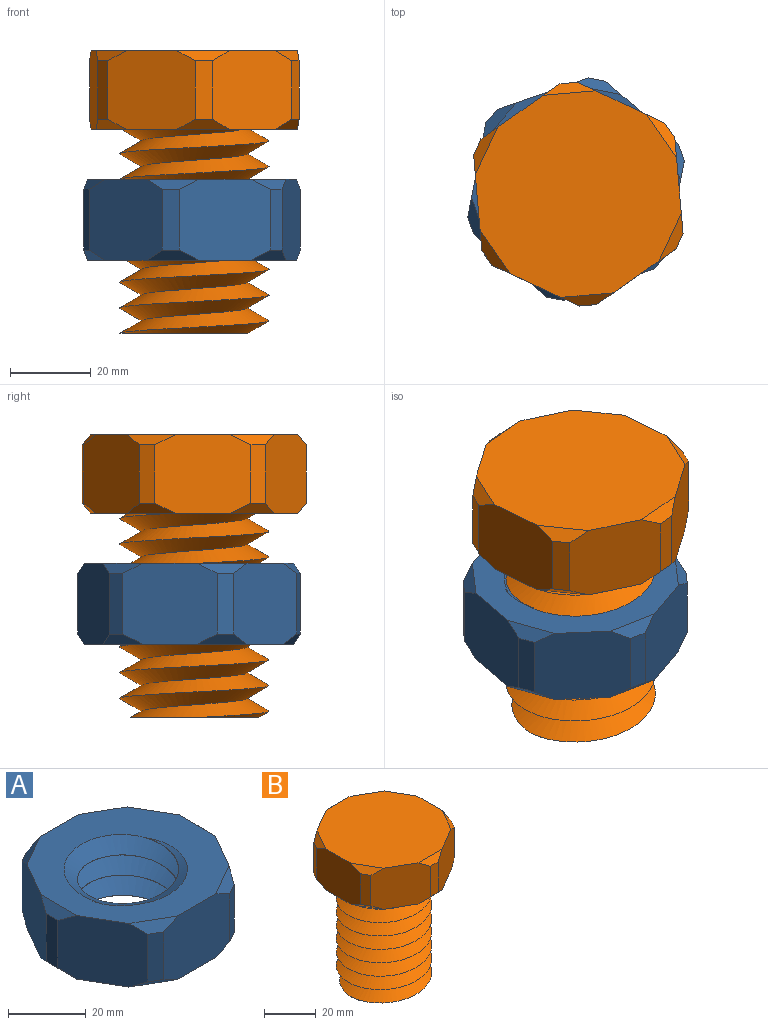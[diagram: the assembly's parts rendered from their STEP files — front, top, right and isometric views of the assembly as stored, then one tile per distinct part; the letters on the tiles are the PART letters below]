
ASSEMBLY  parts=2 mates=1
PART A: 29 faces, bbox 55.2x50x27.6 mm
  f0: cylinder r=13mm len=26mm, axis (0,0,-1), area 3.5mm2, adj f1,f2,f9,f10
  f1: bspline ~42.72x37mm, area 1977mm2, adj f0,f2,f9,f10
  f2: bspline ~42.72x37mm, area 1977.1mm2, adj f0,f1,f9,f10
  f3: plane 20.67x20mm, normal (0.87,-0.5,0), area 452.4mm2, adj f9,f10,f13,f14,f19,f20,f26,f27
  f4: plane 20.67x20mm, normal (0.87,0.5,0), area 452.4mm2, adj f9,f10,f12,f13,f18,f19,f25,f26
  f5: plane 23.87x20mm, normal (0,1,0), area 452.4mm2, adj f9,f10,f11,f12,f17,f18,f24,f25
  f6: plane 20.67x20mm, normal (-0.87,0.5,0), area 452.4mm2, adj f9,f10,f11,f15,f17,f22,f23,f24
  f7: plane 20.67x20mm, normal (-0.87,-0.5,0), area 452.4mm2, adj f9,f10,f15,f16,f21,f22,f23,f28
  f8: plane 23.87x20mm, normal (0,-1,0), area 452.4mm2, adj f9,f10,f14,f16,f20,f21,f27,f28
  f9: plane 50.24x50mm, normal (0,0,1), area 1232.2mm2, adj f0,f1,f2,f3,f4,f5,f6,f7
  f10: plane 50.24x50mm, normal (0,0,-1), area 1232.4mm2, adj f0,f1,f2,f3,f4,f5,f6,f7
  f11: plane 15x3.75mm, normal (-0.5,0.87,0), area 65mm2, adj f5,f6,f17,f24
  f12: plane 15x3.75mm, normal (0.5,0.87,0), area 65mm2, adj f4,f5,f18,f25
  f13: plane 15x4.33mm, normal (1,0,0), area 65mm2, adj f3,f4,f19,f26
  f14: plane 15x3.75mm, normal (0.5,-0.87,0), area 65mm2, adj f3,f8,f20,f27
  f15: plane 15x4.33mm, normal (-1,0,0), area 65mm2, adj f6,f7,f22,f23
  f16: plane 15x3.75mm, normal (-0.5,-0.87,0), area 65mm2, adj f7,f8,f21,f28
  f17: plane 11.25x6.5mm, normal (-0.35,0.61,-0.71), area 30.6mm2, adj f5,f6,f10,f11
  f18: plane 11.25x6.5mm, normal (0.35,0.61,-0.71), area 30.6mm2, adj f4,f5,f10,f12
  f19: plane 12.99x2.5mm, normal (0.71,0,-0.71), area 30.6mm2, adj f3,f4,f10,f13
  f20: plane 11.25x6.5mm, normal (0.35,-0.61,-0.71), area 30.6mm2, adj f3,f8,f10,f14
  f21: plane 11.25x6.5mm, normal (-0.35,-0.61,-0.71), area 30.6mm2, adj f7,f8,f10,f16
  f22: plane 12.99x2.5mm, normal (-0.71,0,-0.71), area 30.6mm2, adj f6,f7,f10,f15
  f23: plane 12.99x2.5mm, normal (-0.71,0,0.71), area 30.6mm2, adj f6,f7,f9,f15
  f24: plane 11.25x6.5mm, normal (-0.35,0.61,0.71), area 30.6mm2, adj f5,f6,f9,f11
  f25: plane 11.25x6.5mm, normal (0.35,0.61,0.71), area 30.6mm2, adj f4,f5,f9,f12
  f26: plane 12.99x2.5mm, normal (0.71,0,0.71), area 30.6mm2, adj f3,f4,f9,f13
  f27: plane 11.25x6.5mm, normal (0.35,-0.61,0.71), area 30.6mm2, adj f3,f8,f9,f14
  f28: plane 11.25x6.5mm, normal (-0.35,-0.61,0.71), area 30.6mm2, adj f7,f8,f9,f16
PART B: 30 faces, bbox 50x55.2x74.2 mm
  f0: plane 20.67x19.5mm, normal (0.5,-0.87,0), area 440.4mm2, adj f6,f11,f14,f15,f22,f23,f28,f29
  f1: plane 23.87x19.5mm, normal (1,0,0), area 440.4mm2, adj f6,f11,f13,f14,f21,f23,f27,f28
  f2: plane 20.67x19.5mm, normal (0.5,0.87,0), area 440.4mm2, adj f6,f11,f12,f13,f20,f21,f26,f27
  f3: plane 20.67x19.5mm, normal (-0.5,0.87,0), area 440.4mm2, adj f6,f11,f12,f16,f19,f20,f25,f26
  f4: plane 23.87x19.5mm, normal (-1,0,0), area 440.4mm2, adj f6,f11,f16,f17,f18,f19,f24,f25
  f5: plane 20.67x19.5mm, normal (-0.5,-0.87,0), area 440.4mm2, adj f6,f11,f15,f17,f18,f22,f24,f29
  f6: plane 50.24x50mm, normal (0,0,-1), area 1232.3mm2, adj f0,f1,f2,f3,f4,f5,f8,f9
  f7: plane 31.7x31.6mm, normal (0,0,-1), area 786.6mm2, adj f8,f9,f10
  f8: bspline ~58.33x42.72mm, area 5003mm2, adj f6,f7,f9,f10
  f9: bspline ~57.27x42.72mm, area 5004.2mm2, adj f6,f7,f8,f10
  f10: cylinder r=13mm len=50.5mm, axis (0,0,1), area 25.1mm2, adj f6,f7,f8,f9
  f11: plane 50.24x50mm, normal (0,0,1), area 2018.9mm2, adj f0,f1,f2,f3,f4,f5,f24,f25
  f12: plane 14.5x4.33mm, normal (0,1,0), area 62.8mm2, adj f2,f3,f20,f26
  f13: plane 14.5x3.75mm, normal (0.87,0.5,0), area 62.8mm2, adj f1,f2,f21,f27
  f14: plane 14.5x3.75mm, normal (0.87,-0.5,0), area 62.8mm2, adj f0,f1,f23,f28
  f15: plane 14.5x4.33mm, normal (0,-1,0), area 62.8mm2, adj f0,f5,f22,f29
  f16: plane 14.5x3.75mm, normal (-0.87,0.5,0), area 62.8mm2, adj f3,f4,f19,f25
  f17: plane 14.5x3.75mm, normal (-0.87,-0.5,0), area 62.8mm2, adj f4,f5,f18,f24
  f18: plane 11.25x6.5mm, normal (-0.61,-0.35,-0.71), area 30.6mm2, adj f4,f5,f6,f17
  f19: plane 11.25x6.5mm, normal (-0.61,0.35,-0.71), area 30.6mm2, adj f3,f4,f6,f16
  f20: plane 12.99x2.5mm, normal (0,0.71,-0.71), area 30.6mm2, adj f2,f3,f6,f12
  f21: plane 11.25x6.5mm, normal (0.61,0.35,-0.71), area 30.6mm2, adj f1,f2,f6,f13
  f22: plane 12.99x2.5mm, normal (0,-0.71,-0.71), area 30.6mm2, adj f0,f5,f6,f15
  f23: plane 11.25x6.5mm, normal (0.61,-0.35,-0.71), area 30.6mm2, adj f0,f1,f6,f14
  f24: plane 11.25x6.5mm, normal (-0.61,-0.35,0.71), area 30.6mm2, adj f4,f5,f11,f17
  f25: plane 11.25x6.5mm, normal (-0.61,0.35,0.71), area 30.6mm2, adj f3,f4,f11,f16
  f26: plane 12.99x2.5mm, normal (0,0.71,0.71), area 30.6mm2, adj f2,f3,f11,f12
  f27: plane 11.25x6.5mm, normal (0.61,0.35,0.71), area 30.6mm2, adj f1,f2,f11,f13
  f28: plane 11.25x6.5mm, normal (0.61,-0.35,0.71), area 30.6mm2, adj f0,f1,f11,f14
  f29: plane 12.99x2.5mm, normal (0,-0.71,0.71), area 30.6mm2, adj f0,f5,f11,f15
PLACE A rot(axis=(-0.94,0.35,0),180deg) t=(-134.66,31.17,34.83)mm
PLACE B rot(axis=(0,0,1),4.9deg) t=(-54.29,-39.29,22.19)mm
MATE cylindrical A.f9 <-> B.f10  axis (0,0,-1) through (-54.29,-39.29,-10.17)mm
